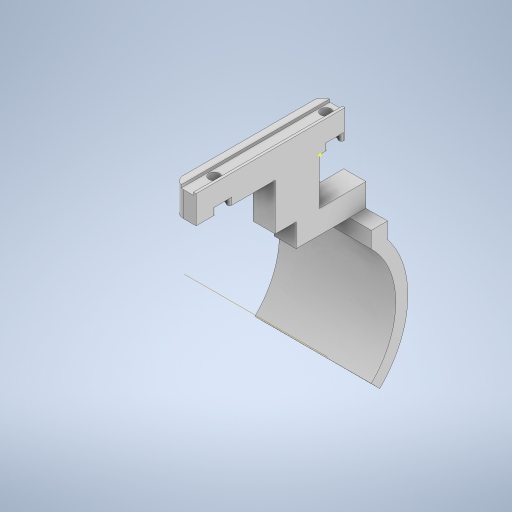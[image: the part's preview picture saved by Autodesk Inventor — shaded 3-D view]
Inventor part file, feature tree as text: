
AUTODESK INVENTOR PART (.ipt)
format: ipt  version: 2024 (Build 280153000, 153)  size: 393,728 bytes
history: native  units: in
note: dims shown in document units (in); Inventor stores cm internally (conversion verified against a paired STEP export)
features: sketch x11, extrude x7, projected_geometry x4, fillet x2, sweep x1, other x1, revolve x1
ambient origin geometry x8: Origin, YZ Plane, XZ Plane, XY Plane, X Axis, Y Axis, Z Axis, Center Point
bodies: Solid1 (feature_tree)
feature tree (27):
  extrude  "Extrusion1"  Depth=2.5197in
  extrude  "Extrusion2"  Depth=1.8898in
  extrude  "Extrusion3"  Depth=0.4724in TaperAngle=0.0deg
  fillet  "Fillet1"  Radius=0.0433in
  fillet  "Fillet2"  Radius=0.2126in
  extrude  "Extrusion19"  Depth=0.4724in TaperAngle=0.0deg
  extrude  "Extrusion21"  Depth=0.1181in TaperAngle=0.0deg
  sketch  "Sketch41"  dims[d17=0.1772in d18=0.0394in]
  extrude  "Extrusion22"  Depth=0.0394in
  sweep  "Sweep3"
  extrude  "Extrusion23"  Depth=0.748in
  sketch  "Sketch47"  dims[d132=0.3937in d133=0.0in d134=1.2283in d135=180.0deg d136=0.2756in d137=1.9685in d138=0.2756in d139=0.2756in d140=0.0in d141=1.9685in d142=1.378in d143=0.0in d144=0.0in d147=0.3937in d148=0.0in d149=0.0787in d150=90.0deg d42=0.0197in d43=0.0344in d44=0.0197in d45=0.0344in d46=0.0in d47=0.0in d48=0.0in d49=0.0in d50=0.0in d51=0.0in d52=0.0in d53=0.0in d55=0.0197in d56=0.0344in d57=0.0197in d58=0.0344in d60=0.0197in d61=0.0344in d62=0.0197in d63=0.0344in d72=0.0197in d73=0.0344in d74=0.0197in d75=0.0344in]
  other  "Work Axis2"
  revolve  "Revolution2"  [1 undecoded]
  sketch  "Sketch1"  dims[d1=0.374in d2=2.5197in]
  sketch  "Sketch2"  dims[d3=0.1772in d4=1.8898in]
  sketch  "Sketch3"  dims[d6=0.1457in d7=0.4724in d8=0.0in d9=0.0433in d10=0.2126in]
  projected_geometry  "Projected Loop2"
  projected_geometry  "Projected Loop3"
  projected_geometry  "Projected Loop4"
  projected_geometry  "Projected Loop5"
  sketch  "Sketch28"  dims[d11=0.0472in d12=0.4724in d13=0.0in]
  sketch  "Sketch40"  dims[d14=0.2953in d15=0.1181in d16=0.0in]
  sketch  "Sketch42"  dims[d19=0.1575in d76=0.4724in]
  sketch  "Sketch43"  dims[d107=0.102in d108=0.748in]
  sketch  "Sketch44"  dims[d109=0.7874in d110=0.0in d130=0.7874in]
  sketch  "Sketch46"  dims[d131=1.1811in]
note: 1 required parameter value undecoded (feature->parameter linkage not recoverable at this tier; creation-order binding heuristic only, values carry confidence <= 0.55)
